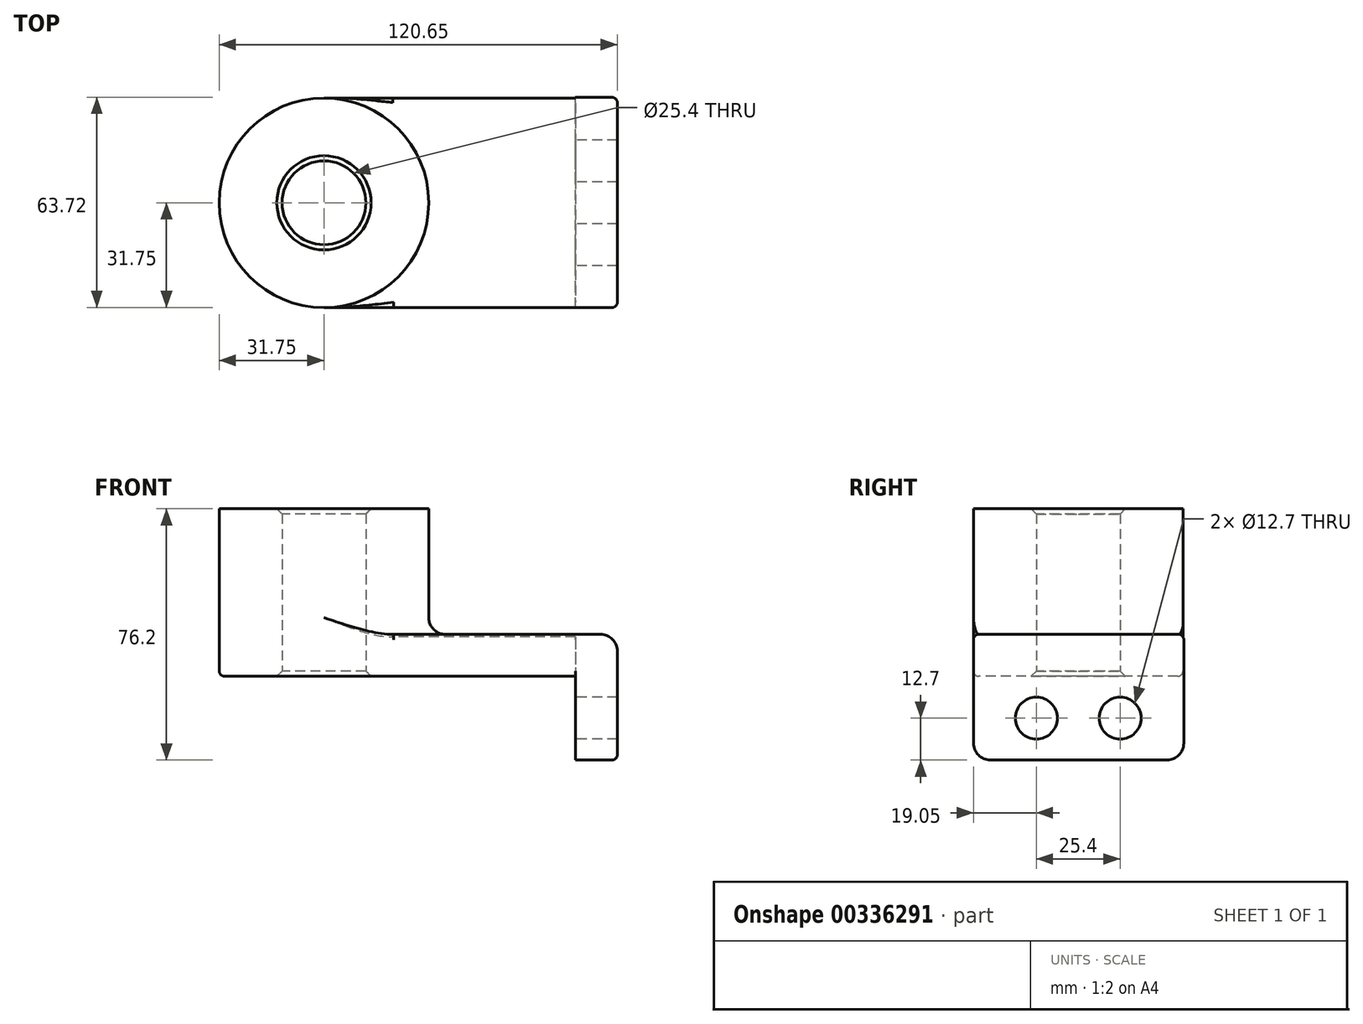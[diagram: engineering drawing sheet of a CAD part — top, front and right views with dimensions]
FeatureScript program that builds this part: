
annotation { "Feature Type Name" : "Feature", "Feature Type Description" : "" }
export const myFeature = defineFeature(function(context is Context, id is Id, definition is map)
    precondition{}
    {
        {
            var Q0;
            Q0=qCreatedBy(makeId("Top.planeOp"),FACE);
            var sketch = newSketch(context, id + "F0", { "sketchPlane" : qUnion([Q0])});
            skLineSegment(sketch, "E0.bottom", {"start": v(-38.1, 31.75) * mm, "end": v(38.1, 31.75) * mm});
            skLineSegment(sketch, "E0.top", {"start": v(-38.1, -31.75) * mm, "end": v(38.1, -31.75) * mm});
            skLineSegment(sketch, "E0.left", {"start": v(-38.1, 31.75) * mm, "end": v(-38.1, -31.75) * mm});
            skLineSegment(sketch, "E0.right", {"start": v(38.1, 31.75) * mm, "end": v(38.1, -31.75) * mm});
            skPoint(sketch, "E0.middle", {"position": v(0, 0) * mm});
            skCircle(sketch, "E1", {"center": v(-38.1, 0) * mm, "radius": 31.75 * mm});
            skCircle(sketch, "E2", {"center": v(-38.1, 0) * mm, "radius": 12.7 * mm});
            skSolve(sketch);
        }
        {
            var Q0;
            Q0 = qSketchRegion(id + "F0", true);
            extrude(context, id + "F1", {"entities" : qUnion([Q0]), "depth" : 12.7 * mm});
        }
        {
            var Q0;
            {var subQ1=sQuery(id+"F0.wireOp",EDGE,"E0.left");var subQ3=sQuery(id+"F0.wireOp",EDGE,"E2");var subQ4=makeQuery(id+"F0.imprint","INTERSECT",VERTEX,{"disambiguationData":[OD(0.0)],"derivedFrom":[subQ1,subQ3]});Q0=makeQuery(id+"F0.imprint","IMPRINT",FACE,{"disambiguationData":[TD([[makeQuery(id+"F0.imprint","IMPRINT",EDGE,{"disambiguationData":[TD([[subQ4,1.0]])],"derivedFrom":subQ3}),-1.0]])]});}
            var Q1;
            {var subQ1=sQuery(id+"F0.wireOp",EDGE,"E0.left");var subQ3=sQuery(id+"F0.wireOp",EDGE,"E2");var subQ4=makeQuery(id+"F0.imprint","INTERSECT",VERTEX,{"disambiguationData":[OD(0.0)],"derivedFrom":[subQ1,subQ3]});Q1=makeQuery(id+"F0.imprint","IMPRINT",FACE,{"disambiguationData":[TD([[makeQuery(id+"F0.imprint","IMPRINT",EDGE,{"disambiguationData":[TD([[subQ4,-1.0]])],"derivedFrom":subQ3}),-1.0]])]});}
            extrude(context, id + "F2", {"entities" : qUnion([Q0, Q1]), "operationType" : NewBodyOperationType.ADD, "depth" : 50.8 * mm});
        }
        {
            var Q0;
            Q0=makeQuery(id+"F1.opExtrude","SWEPT_FACE",FACE,{"disambiguationData":[OSD([sQuery(id+"F0.wireOp",EDGE,"E0.right")])]});
            var sketch = newSketch(context, id + "F3", { "sketchPlane" : qUnion([Q0])});
            skLineSegment(sketch, "E3.bottom", {"start": v(-31.75, 12.7) * mm, "end": v(31.97, 12.7) * mm});
            skLineSegment(sketch, "E3.top", {"start": v(-31.75, -25.4) * mm, "end": v(31.97, -25.4) * mm});
            skLineSegment(sketch, "E3.left", {"start": v(-31.75, 12.7) * mm, "end": v(-31.75, -25.4) * mm});
            skLineSegment(sketch, "E3.right", {"start": v(31.97, 12.7) * mm, "end": v(31.97, -25.4) * mm});
            skCircle(sketch, "E4", {"center": v(-12.7, -12.7) * mm, "radius": 6.35 * mm});
            skLineSegment(sketch, "E5", {"start": v(0, 0) * mm, "end": v(0, -25.4) * mm});
            skCircle(sketch, "E6.MirrorC", {"center": v(12.7, -12.7) * mm, "radius": 6.35 * mm});
            skSolve(sketch);
        }
        {
            var Q0;
            Q0 = qSketchRegion(id + "F3", true);
            extrude(context, id + "F4", {"entities" : qUnion([Q0]), "operationType" : NewBodyOperationType.ADD, "depth" : 12.7 * mm});
        }
        {
            var Q0;
            {var subQ0=sQuery(id+"F0.wireOp",EDGE,"E1");Q0=makeQuery(id+"F2.boolean.opBoolean","INTERSECT",EDGE,{"derivedFrom":[makeQuery(id+"F1.opExtrude","CAP_FACE",FACE,{"disambiguationData":[OSD([sQuery(id+"F0.wireOp",EDGE,"E0.bottom"),sQuery(id+"F0.wireOp",EDGE,"E0.top"),sQuery(id+"F0.wireOp",EDGE,"E0.right"),subQ0,sQuery(id+"F0.wireOp",EDGE,"E2")])],"isStart":false}),makeQuery(id+"F2.opExtrude","SWEPT_FACE",FACE,{"disambiguationData":[OSD([subQ0])]})]});}
            var Q1;
            Q1=makeQuery(id+"F4.opExtrude","CAP_EDGE",EDGE,{"disambiguationData":[OSD([sQuery(id+"F3.wireOp",EDGE,"E3.bottom")])],"isStart":false});
            var Q2;
            Q2=makeQuery(id+"F4.opExtrude","SWEPT_EDGE",EDGE,{"disambiguationData":[OSD([sQuery(id+"F3.wireOp",EDGE,"E3.top"),sQuery(id+"F3.wireOp",EDGE,"E3.left")])]});
            var Q3;
            Q3=makeQuery(id+"F4.opExtrude","SWEPT_EDGE",EDGE,{"disambiguationData":[OSD([sQuery(id+"F3.wireOp",EDGE,"E3.top"),sQuery(id+"F3.wireOp",EDGE,"E3.right")])]});
            fillet(context, id + "F5", {"entities" : qUnion([Q0, Q1, Q2, Q3]), "radius" : 5.08 * mm, "tangentPropagation" : true, "allowEdgeOverflow" : false});
        }
        {
            var Q0;
            Q0=makeQuery(id+"F4.boolean.opBoolean","MERGE",EDGE,{"derivedFrom":[makeQuery(id+"F1.opExtrude","CAP_EDGE",EDGE,{"disambiguationData":[OSD([sQuery(id+"F0.wireOp",EDGE,"E0.top")])],"isStart":false}),makeQuery(id+"F4.opExtrude","SWEPT_EDGE",EDGE,{"disambiguationData":[OSD([sQuery(id+"F3.wireOp",EDGE,"E3.bottom"),sQuery(id+"F3.wireOp",EDGE,"E3.left")])]})]});
            var Q1;
            Q1=makeQuery(id+"F1.opExtrude","CAP_EDGE",EDGE,{"disambiguationData":[OSD([sQuery(id+"F0.wireOp",EDGE,"E0.top")])],"isStart":true});
            fillet(context, id + "F6", {"entities" : qUnion([Q0, Q1]), "radius" : 1.59 * mm, "tangentPropagation" : true, "allowEdgeOverflow" : false});
        }
        {
            var Q0;
            {var subQ0=sQuery(id+"F0.wireOp",EDGE,"E2");Q0=makeQuery(id+"F2.boolean.opBoolean","MERGE",FACE,{"derivedFrom":[makeQuery(id+"F1.opExtrude","SWEPT_FACE",FACE,{"disambiguationData":[OSD([subQ0])]}),makeQuery(id+"F2.opExtrude","SWEPT_FACE",FACE,{"disambiguationData":[OSD([subQ0])]})]});}
            chamfer(context, id + "F7", {"entities" : qUnion([Q0]), "width" : 1.59 * mm, "tangentPropagation" : true});
        }
    });
